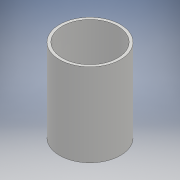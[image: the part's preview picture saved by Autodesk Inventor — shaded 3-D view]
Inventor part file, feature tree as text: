
AUTODESK INVENTOR PART (.ipt)
format: ipt  version: 2017 (Build 210142000, 142)  size: 94,208 bytes
history: native  units: mm
features: extrude x1, sketch x1
ambient origin geometry x8: Origin, YZ Plane, XZ Plane, XY Plane, X Axis, Y Axis, Z Axis, Center Point
bodies: Body1 (feature_tree)
feature tree (2):
  extrude  "Extrusion2"  Depth=30.0mm
  sketch  "Sketch2"  dims[d5=22.0mm d7=1.0mm d8=30.0mm d9=0.0mm]
